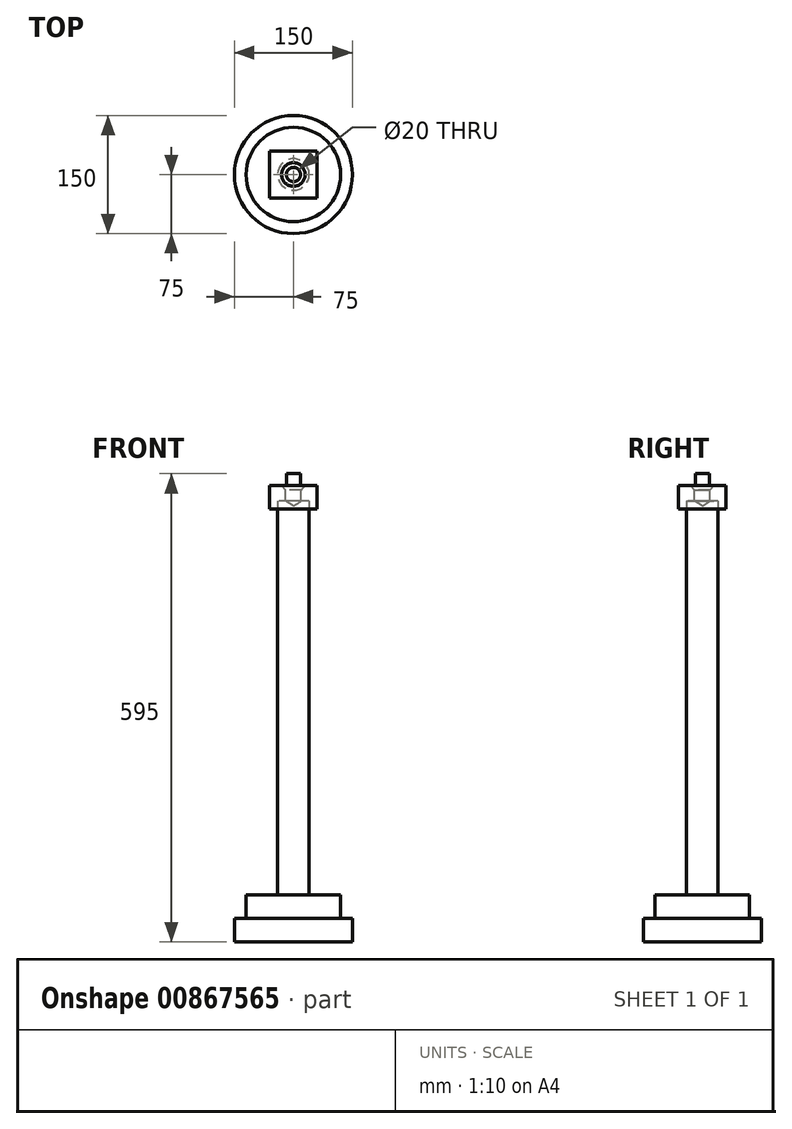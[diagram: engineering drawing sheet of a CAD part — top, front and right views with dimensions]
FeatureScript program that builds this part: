
annotation { "Feature Type Name" : "Feature", "Feature Type Description" : "" }
export const myFeature = defineFeature(function(context is Context, id is Id, definition is map)
    precondition{}
    {
        {
            var Q0;
            Q0=qCreatedBy(makeId("Top.planeOp"),FACE);
            var sketch = newSketch(context, id + "F0", { "sketchPlane" : qUnion([Q0])});
            skCircle(sketch, "E0", {"center": v(0, 0) * mm, "radius": 75 * mm});
            skSolve(sketch);
        }
        {
            var Q0;
            Q0 = qSketchRegion(id + "F0", true);
            extrude(context, id + "F1", {"entities" : qUnion([Q0]), "depth" : 30 * mm, "offsetDistance" : 25 * mm});
        }
        {
            var Q0;
            Q0=makeQuery(id+"F1.opExtrude","CAP_FACE",FACE,{"disambiguationData":[OSD([sQuery(id+"F0.wireOp",EDGE,"E0")])],"isStart":false});
            var sketch = newSketch(context, id + "F2", { "sketchPlane" : qUnion([Q0])});
            skCircle(sketch, "E1", {"center": v(0, 0) * mm, "radius": 60 * mm});
            skSolve(sketch);
        }
        {
            var Q0;
            Q0=makeQuery(id+"F2.imprint","IMPRINT",FACE,{"disambiguationData":[TD([[makeQuery(id+"F2.imprint","IMPRINT",EDGE,{"derivedFrom":sQuery(id+"F2.wireOp",EDGE,"E1")}),1.0]])]});
            extrude(context, id + "F3", {"entities" : qUnion([Q0]), "operationType" : NewBodyOperationType.ADD, "depth" : 30 * mm, "offsetDistance" : 25 * mm});
        }
        {
            var Q0;
            Q0=makeQuery(id+"F3.opExtrude","CAP_FACE",FACE,{"disambiguationData":[OSD([sQuery(id+"F2.wireOp",EDGE,"E1")])],"isStart":false});
            var sketch = newSketch(context, id + "F4", { "sketchPlane" : qUnion([Q0])});
            skCircle(sketch, "E2", {"center": v(0, 0) * mm, "radius": 20 * mm});
            skSolve(sketch);
        }
        {
            var Q0;
            Q0 = qSketchRegion(id + "F4", true);
            var Q1;
            Q1=makeQuery(id+"F1.opExtrude","CAP_FACE",FACE,{"disambiguationData":[OSD([sQuery(id+"F0.wireOp",EDGE,"E0")])],"isStart":true});
            extrude(context, id + "F5", {"entities" : qUnion([Q0]), "operationType" : NewBodyOperationType.ADD, "depth" : 500 * mm, "endBoundEntityFace" : qUnion([Q1]), "offsetDistance" : 25 * mm});
        }
        {
            var Q0;
            Q0=makeQuery(id+"F5.opExtrude","CAP_FACE",FACE,{"disambiguationData":[OSD([sQuery(id+"F4.wireOp",EDGE,"E2")])],"isStart":false});
            cPlane(context, id + "F6", {"entities" : qUnion([Q0]), "cplaneType" : CPlaneType.OFFSET, "offset" : 20 * mm, "width" : 150 * mm, "height" : 150 * mm});
        }
        {
            var Q0;
            Q0=qCreatedBy(id+"F6.planeOp",FACE);
            var sketch = newSketch(context, id + "F7", { "sketchPlane" : qUnion([Q0])});
            skLineSegment(sketch, "E3.bottom", {"start": v(-30, 30) * mm, "end": v(30, 30) * mm});
            skLineSegment(sketch, "E3.top", {"start": v(-30, -30) * mm, "end": v(30, -30) * mm});
            skLineSegment(sketch, "E3.left", {"start": v(-30, 30) * mm, "end": v(-30, -30) * mm});
            skLineSegment(sketch, "E3.right", {"start": v(30, 30) * mm, "end": v(30, -30) * mm});
            skPoint(sketch, "E3.middle", {"position": v(0, 0) * mm});
            skSolve(sketch);
        }
        {
            var Q0;
            Q0 = qSketchRegion(id + "F7", true);
            extrude(context, id + "F8", {"entities" : qUnion([Q0]), "oppositeDirection" : true, "depth" : 30 * mm, "offsetDistance" : 25 * mm});
        }
        {
            var Q0;
            Q0=makeQuery(id+"F8.opExtrude","CAP_FACE",FACE,{"disambiguationData":[OSD([sQuery(id+"F7.wireOp",EDGE,"E3.bottom"),sQuery(id+"F7.wireOp",EDGE,"E3.top"),sQuery(id+"F7.wireOp",EDGE,"E3.left"),sQuery(id+"F7.wireOp",EDGE,"E3.right")])],"isStart":true});
            var sketch = newSketch(context, id + "F9", { "sketchPlane" : qUnion([Q0])});
            skPoint(sketch, "E4", {"position": v(0, 0) * mm});
            skSolve(sketch);
        }
        {
            var Q0;
            Q0=sQuery(id+"F9.wireOp",VERTEX,"E4");
            var Q1;
            Q1=makeQuery(id+"F8.opExtrude","SWEPT_BODY",BODY,{"disambiguationData":[OSD([sQuery(id+"F7.wireOp",EDGE,"E3.bottom"),sQuery(id+"F7.wireOp",EDGE,"E3.top"),sQuery(id+"F7.wireOp",EDGE,"E3.left"),sQuery(id+"F7.wireOp",EDGE,"E3.right")])]});
            hole(context, id + "F10", {"style" : HoleStyle.C_SINK, "endStyle" : HoleEndStyle.BLIND, "holeDiameter" : 20 * mm, "cSinkDiameter" : 30 * mm, "cSinkAngle" : 82 * degree, "majorDiameter" : 5 * mm, "holeDepth" : 20 * mm, "isTappedThrough" : true, "tappedDepth" : 12 * mm, "tapClearance" : 3, "locations" : qUnion([Q0]), "scope" : qUnion([Q1])});
        }
        {
            var Q0;
            Q0=makeQuery(id+"F8.opExtrude","CAP_FACE",FACE,{"disambiguationData":[OSD([sQuery(id+"F7.wireOp",EDGE,"E3.bottom"),sQuery(id+"F7.wireOp",EDGE,"E3.top"),sQuery(id+"F7.wireOp",EDGE,"E3.left"),sQuery(id+"F7.wireOp",EDGE,"E3.right")])],"isStart":true});
            var sketch = newSketch(context, id + "F11", { "sketchPlane" : qUnion([Q0])});
            skCircle(sketch, "E5.0", {"center": v(0, 0) * mm, "radius": 15 * mm});
            skSolve(sketch);
        }
        {
            var Q0;
            Q0 = qSketchRegion(id + "F11", true);
            var Q1;
            Q1=makeQuery(id+"F8.opExtrude","CAP_FACE",FACE,{"disambiguationData":[OSD([sQuery(id+"F7.wireOp",EDGE,"E3.bottom"),sQuery(id+"F7.wireOp",EDGE,"E3.top"),sQuery(id+"F7.wireOp",EDGE,"E3.left"),sQuery(id+"F7.wireOp",EDGE,"E3.right")])],"isStart":false});
            extrude(context, id + "F12", {"entities" : qUnion([Q0]), "endBound" : BoundingType.UP_TO_SURFACE, "oppositeDirection" : true, "depth" : 25 * mm, "endBoundEntityFace" : qUnion([Q1]), "offsetDistance" : 25 * mm});
        }
        {
            var Q0;
            Q0=makeQuery(id+"F12.opExtrude","CAP_FACE",FACE,{"disambiguationData":[OSD([sQuery(id+"F11.wireOp",EDGE,"E5.0")])],"isStart":true});
            var sketch = newSketch(context, id + "F13", { "sketchPlane" : qUnion([Q0])});
            skCircle(sketch, "E6", {"center": v(0, 0) * mm, "radius": 9 * mm});
            skSolve(sketch);
        }
        {
            var Q0;
            Q0 = qSketchRegion(id + "F13", true);
            extrude(context, id + "F14", {"entities" : qUnion([Q0]), "operationType" : NewBodyOperationType.ADD, "depth" : 15 * mm, "offsetDistance" : 25 * mm});
        }
        {
            var Q0;
            Q0=makeQuery(id+"F8.opExtrude","SWEPT_BODY",BODY,{"disambiguationData":[OSD([sQuery(id+"F7.wireOp",EDGE,"E3.bottom"),sQuery(id+"F7.wireOp",EDGE,"E3.top"),sQuery(id+"F7.wireOp",EDGE,"E3.left"),sQuery(id+"F7.wireOp",EDGE,"E3.right")])]});
            var Q1;
            Q1=makeQuery(id+"F12.opExtrude","SWEPT_BODY",BODY,{"disambiguationData":[OSD([sQuery(id+"F11.wireOp",EDGE,"E5.0")])]});
            booleanBodies(context, id + "F15", {"operationType" : BooleanOperationType.SUBTRACTION, "tools" : qUnion([Q0]), "targets" : qUnion([Q1]), "keepTools" : true});
        }
    });
